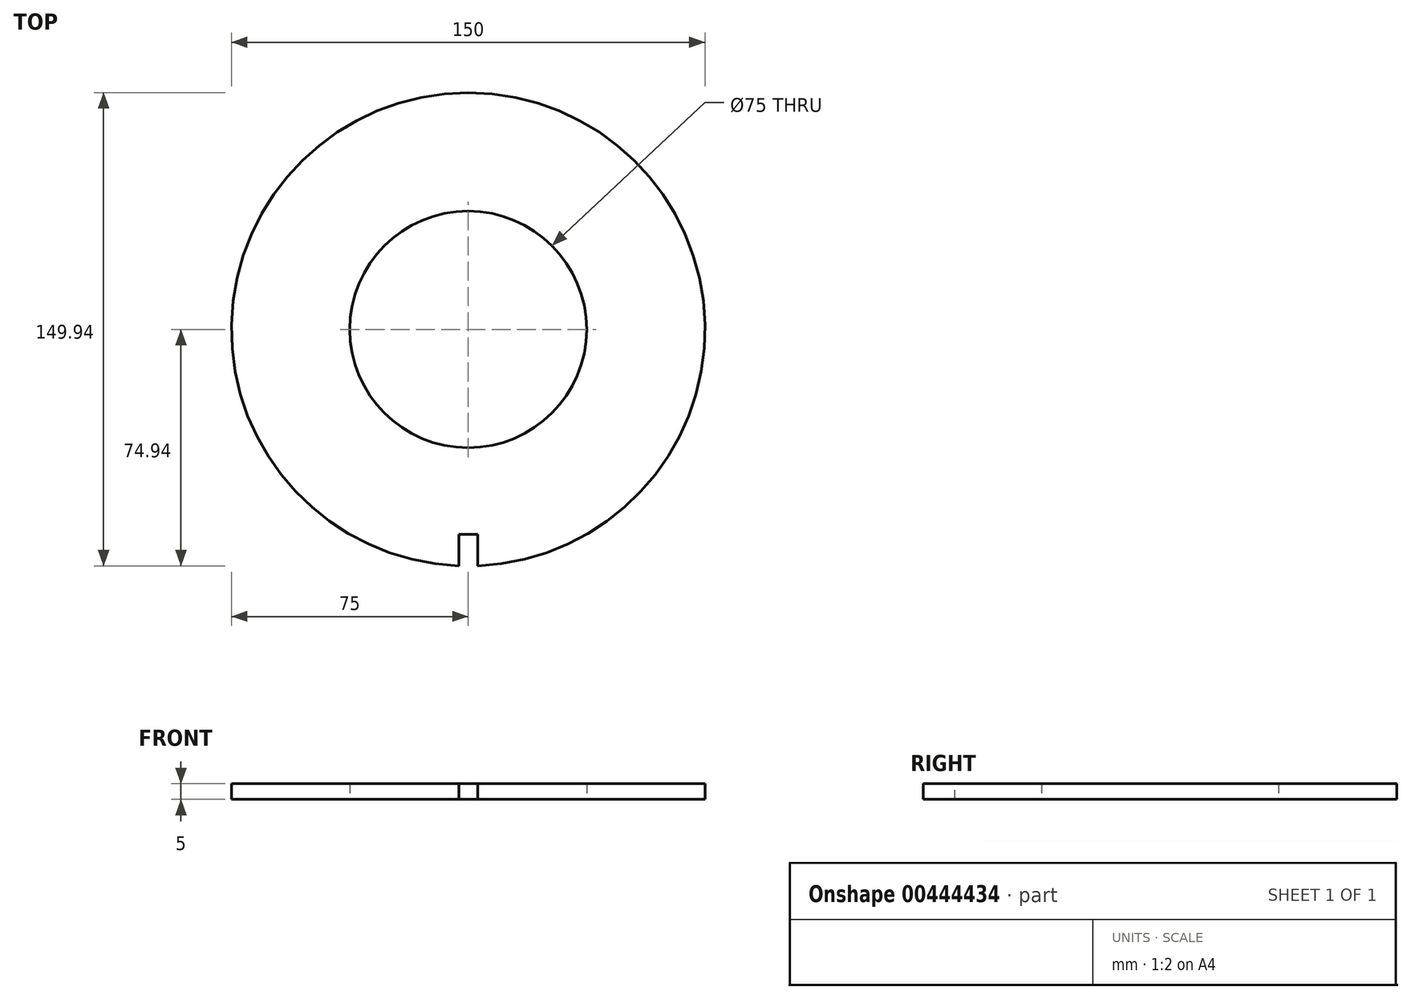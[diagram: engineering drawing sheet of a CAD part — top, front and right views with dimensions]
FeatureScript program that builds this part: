
annotation { "Feature Type Name" : "Feature", "Feature Type Description" : "" }
export const myFeature = defineFeature(function(context is Context, id is Id, definition is map)
    precondition{}
    {
        {
            var Q0;
            Q0=qCreatedBy(makeId("Top.planeOp"),FACE);
            var sketch = newSketch(context, id + "F0", { "sketchPlane" : qUnion([Q0])});
            skCircle(sketch, "E0", {"center": v(0, 0) * mm, "radius": 37.5 * mm});
            skCircle(sketch, "E1", {"center": v(0, 0) * mm, "radius": 75 * mm});
            skSolve(sketch);
        }
        {
            var Q0;
            Q0=makeQuery(id+"F0.imprint","IMPRINT",FACE,{"disambiguationData":[TD([[makeQuery(id+"F0.imprint","IMPRINT",EDGE,{"derivedFrom":sQuery(id+"F0.wireOp",EDGE,"E0")}),-1.0]])]});
            extrude(context, id + "F1", {"entities" : qUnion([Q0]), "depth" : 5 * mm, "offsetDistance" : 25 * mm});
        }
        {
            var Q0;
            Q0=makeQuery(id+"F1.opExtrude","CAP_FACE",FACE,{"disambiguationData":[OSD([sQuery(id+"F0.wireOp",EDGE,"E0"),sQuery(id+"F0.wireOp",EDGE,"E1")])],"isStart":false});
            var sketch = newSketch(context, id + "F2", { "sketchPlane" : qUnion([Q0])});
            skLineSegment(sketch, "E2.bottom", {"start": v(3, -52.4) * mm, "end": v(2.95, -52.5) * mm});
            skPoint(sketch, "E3.endSnap0", {"position": v(-6.64, -79.7) * mm});
            skPoint(sketch, "E4.orphan", {"position": v(-10.29, -94.4) * mm});
            skPoint(sketch, "E5.start.orphan", {"position": v(41.46, -62.5) * mm});
            skPoint(sketch, "E3.end.orphan", {"position": v(-6.64, -85) * mm});
            skLineSegment(sketch, "E6.bottom", {"start": v(-0.03, -58.75) * mm, "end": v(0, -58.7) * mm});
            skLineSegment(sketch, "E6.left", {"start": v(-3, -65) * mm, "end": v(-3, -75) * mm});
            skLineSegment(sketch, "E6.right", {"start": v(3, -74.94) * mm, "end": v(3, -75) * mm});
            skLineSegment(sketch, "E7", {"start": v(0, 0) * mm, "end": v(0, -75) * mm, "construction": true});
            skLineSegment(sketch, "E8.trimOffspring", {"start": v(2.95, -52.5) * mm, "end": v(3, -52.4) * mm});
            skLineSegment(sketch, "E9.trimOffspring", {"start": v(0, -58.7) * mm, "end": v(-0.03, -58.75) * mm});
            skLineSegment(sketch, "E10", {"start": v(0, -75) * mm, "end": v(3, -74.94) * mm});
            skLineSegment(sketch, "E11", {"start": v(0, -75) * mm, "end": v(-3, -75) * mm});
            skLineSegment(sketch, "E12", {"start": v(-3, -75) * mm, "end": v(-3.01, -74.7) * mm});
            skLineSegment(sketch, "E13", {"start": v(-3, -75) * mm, "end": v(3, -75) * mm});
            skLineSegment(sketch, "E14", {"start": v(3, -75) * mm, "end": v(3, -65) * mm});
            skLineSegment(sketch, "E15", {"start": v(-3, -65) * mm, "end": v(3, -65) * mm});
            skSolve(sketch);
        }
        {
            var Q0;
            Q0 = qSketchRegion(id + "F2", true);
            extrude(context, id + "F3", {"entities" : qUnion([Q0]), "operationType" : NewBodyOperationType.REMOVE, "oppositeDirection" : true, "depth" : 52.7 * mm, "offsetDistance" : 25 * mm});
        }
    });
